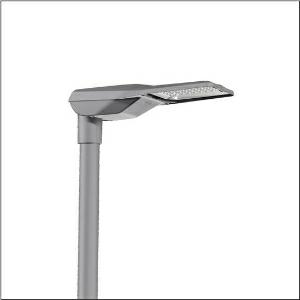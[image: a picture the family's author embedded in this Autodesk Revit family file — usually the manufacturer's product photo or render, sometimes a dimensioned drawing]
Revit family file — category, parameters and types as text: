
# Revit family: streetlight_sl_21_iq_mini___st1_0a_5xe2d31g08jb_707a
name_source: partatom
category: Lighting Fixtures
units: mm (PartAtom-declared; Revit-internal decimal feet)

## family parameters
Cut with Voids When Loaded = No
Host = Face
Light Source = No
Part Type = Normal
Room Calculation Point = No
Round Connector Dimension = Use Diameter
Shared = No

## types (1)
- --- (1 x LED, 10820 lm, 71.6 W, 3000K)
    Apparent Load = 72 VA
    CIE Flux Codes = 40 73 97 100 100
    Color Rendering = 70
    Color Temperature = 3000K
    Default Elevation = 1800 mm
    Description = Streetlight SL 21 iQ mini, mast luminaire, primary light control with lens, of PMMA, primary optical cover: cover, of toughened safety glass, transparent, light distribution: ST1.0a, light emission: direct distribution, primary light characteristic: asymmetric, installation type: post-top, side-entry, LED, High Power LED, rated luminous flux: 10.820lm, luminous efficacy: 151lm/W, light colour: 730, colour temperature: 3000K, control gear: iQ Street-Remote, control: Street-Remote, Auto-Match, Temp-Guard, Lumen-Switch, Night-Set, Smart-Wire, Light-Fading, Desk-Remote (wireless, voltage-free reading and setting of iQ features in the workshop via application-optimized NFC function/RFID function), optimised constant luminous flux control (CLO 2.0), pre-setting: linear dimming characteristic, mains connection: 220..240V, AC, 50/60Hz, start of lifetime: 72W, end of service life: 75W, reduction: 33W, luminaire housing, of diecast aluminium, powder-coated, SITECO metallic grey (DB 702S), corrosivity category C5 high according to DIN EN ISO 12944, please order mast flange separately, inclination adjustable: 0°, 5°, 10°, 15°, sealing non-destructively replaceable, multi-level sealing system, length: 628mm, width: 235mm, height: 110mm, mast flange for spigot size: 42mm (side-entry): 5XC10008XM4, 60/48mm (side-entry/post-top): 5XC10108XM2, 76/60mm (side-entry/post-top): 5XC10108XM1, mounting height: 4..8m, protection rating (complete): IP66, insulation class (complete): insulation class II (safety insulation), certification: CE, ENEC, ENEC+, VDE, impact resistance: IK10, permissible operating ambient temperature for outdoor applications: -40..+50°C, standard-compliant lighting for roads and squares, packaging unit: 1 piece

Light Distribution: ST1.0a
    Height = 110 mm
    Lamp = 1 x LED
    Lamp Light Flux = 10820 lm
    Lamp Power = 71.6 W
    Lamp count = 1
    Length = 625 mm
    Luminous efficacy = 151 lm/W
    Manufacturer = Siteco
    ModVariant = No
    Model = 5XE2D31G08JB
    Number of Poles = 1
    OnlyDefault = Yes
    Power Factor = 1
    Product Name = Streetlight SL 21 iQ mini | ST1.0a
    Product group = mast luminaire | pylon top
    ProductGroupID = 6100
    Protection Class = Protection class II
    Protection Degree = IP 66
    RLX_Detail_Level = 1
    RLX_Emergency_Light_Flux = 0 lm
    RLX_Emergency_Type = 0
    RLX_Emergency_Type_DB = No
    RlxData = <blob elided: 26345 chars, md5=a26c6e8b>
    Socket = socket
    Standby Power = 0 W
    System Light Flux = 10820 lm
    System Power = 72 W
    Type Comments = factory setting: luminous flux: 100 % | dim-lin: 254 | 746 mA
    Type Image = l_1003519.jpg
    URL = http://relux.com
    VarID = @adj_170639
    Voltage = 0 V
    Weight = 0.00 kg
    Width = 234 mm

## geometry (parser evidence)
native form markers: Blend x4, Sweep x10
no freeform markers — native parametric forms only
